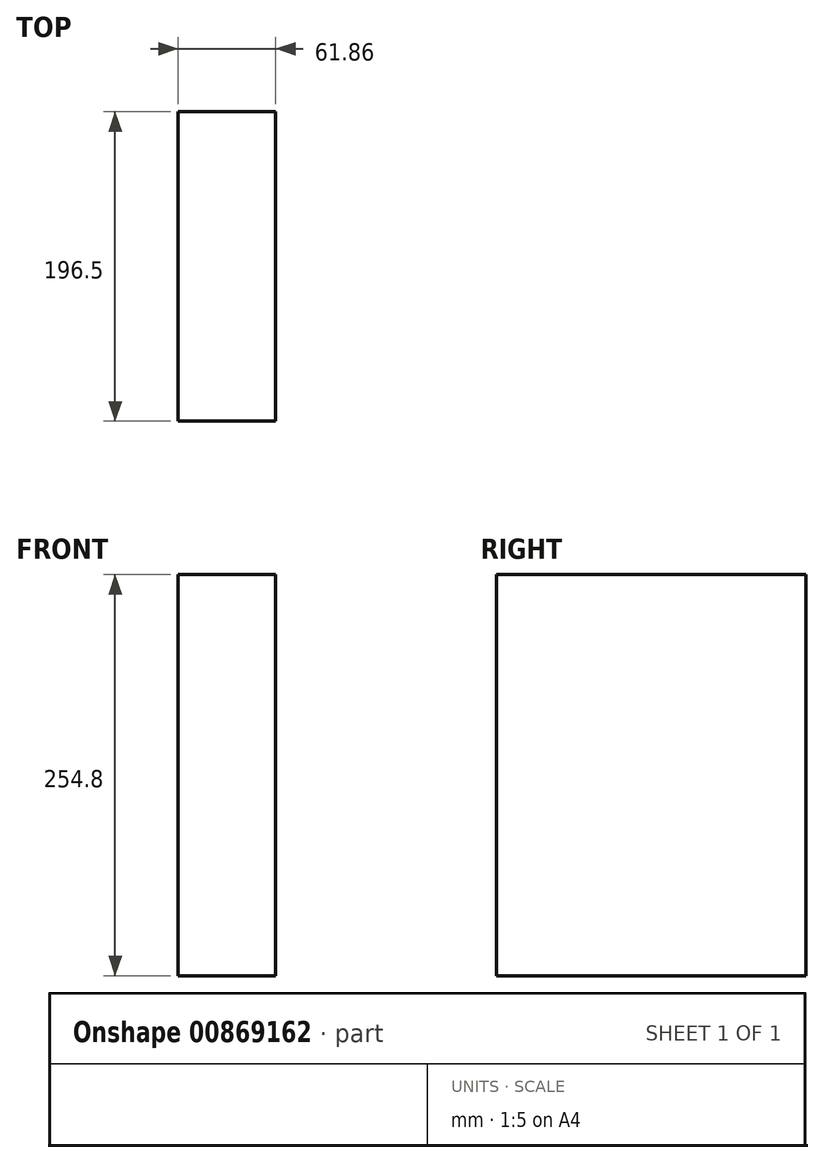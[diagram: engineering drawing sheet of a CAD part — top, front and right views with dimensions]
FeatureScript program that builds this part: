
annotation { "Feature Type Name" : "Feature", "Feature Type Description" : "" }
export const myFeature = defineFeature(function(context is Context, id is Id, definition is map)
    precondition{}
    {
        {
            var Q0;
            Q0=qCreatedBy(makeId("Right.planeOp"),FACE);
            var sketch = newSketch(context, id + "F0", { "sketchPlane" : qUnion([Q0])});
            skLineSegment(sketch, "E0.bottom", {"start": v(98.25, 127.4) * mm, "end": v(-98.25, 127.4) * mm});
            skLineSegment(sketch, "E0.top", {"start": v(98.25, -127.4) * mm, "end": v(-98.25, -127.4) * mm});
            skLineSegment(sketch, "E0.left", {"start": v(98.25, 127.4) * mm, "end": v(98.25, -127.4) * mm});
            skLineSegment(sketch, "E0.right", {"start": v(-98.25, 127.4) * mm, "end": v(-98.25, -127.4) * mm});
            skPoint(sketch, "E0.middle", {"position": v(0, 0) * mm});
            skSolve(sketch);
        }
        {
            var Q0;
            Q0 = qSketchRegion(id + "F0", true);
            extrude(context, id + "F1", {"entities" : qUnion([Q0]), "depth" : 61.86 * mm, "offsetDistance" : 25.4 * mm});
        }
        {
            var Q0;
            Q0=makeQuery(id+"F1.opExtrude","SWEPT_FACE",FACE,{"disambiguationData":[OSD([sQuery(id+"F0.wireOp",EDGE,"E0.bottom")])]});
            var sketch = newSketch(context, id + "F2", { "sketchPlane" : qUnion([Q0])});
            skLineSegment(sketch, "E1", {"start": v(0, -30.5) * mm, "end": v(61.86, -30.5) * mm});
            skLineSegment(sketch, "E2", {"start": v(61.86, -30.5) * mm, "end": v(31.66, -55.65) * mm});
            skLineSegment(sketch, "E3", {"start": v(31.66, -55.65) * mm, "end": v(0, -30.5) * mm});
            skSolve(sketch);
        }
        {
            var Q0;
            Q0=makeQuery(id+"F2.imprint","IMPRINT",FACE,{"disambiguationData":[TD([[makeQuery(id+"F2.imprint","IMPRINT",EDGE,{"derivedFrom":sQuery(id+"F2.wireOp",EDGE,"E1")}),-1.0]])]});
            extrude(context, id + "F3", {"entities" : qUnion([Q0]), "operationType" : NewBodyOperationType.ADD, "oppositeDirection" : true, "depth" : 100.42 * mm, "offsetDistance" : 25.4 * mm});
        }
    });
